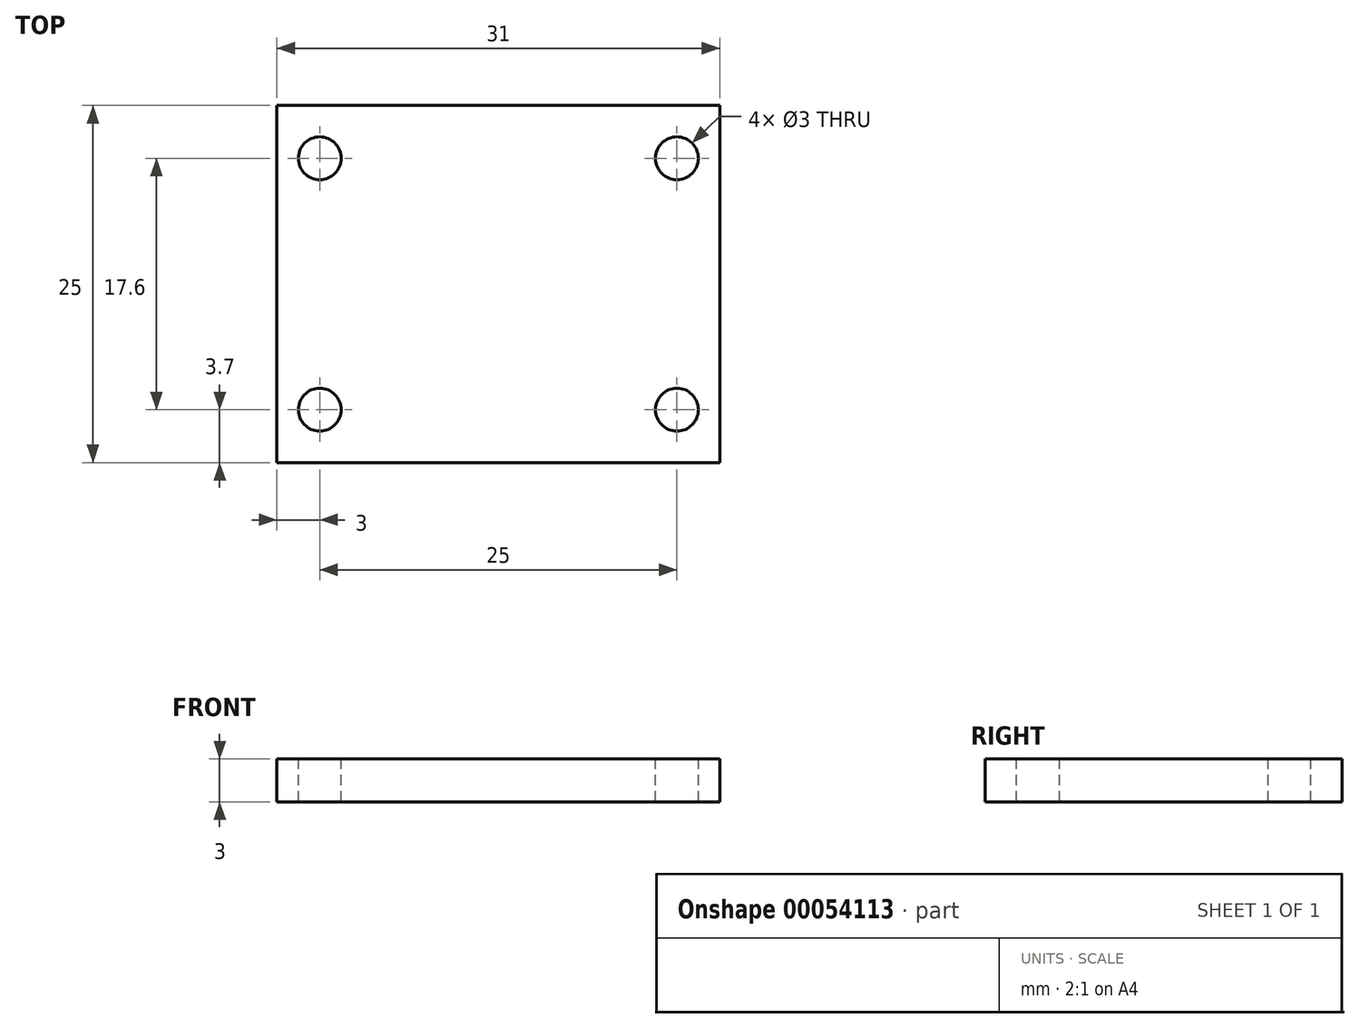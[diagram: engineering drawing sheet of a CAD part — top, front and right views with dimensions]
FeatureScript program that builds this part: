
annotation { "Feature Type Name" : "Feature", "Feature Type Description" : "" }
export const myFeature = defineFeature(function(context is Context, id is Id, definition is map)
    precondition{}
    {
        {
            var Q0;
            Q0=qCreatedBy(makeId("Top.planeOp"),FACE);
            var sketch = newSketch(context, id + "F0", { "sketchPlane" : qUnion([Q0])});
            skLineSegment(sketch, "E0.rect.bottom", {"start": v(15.5, 12.5) * mm, "end": v(-15.5, 12.5) * mm});
            skLineSegment(sketch, "E0.rect.top", {"start": v(15.5, -12.5) * mm, "end": v(-15.5, -12.5) * mm});
            skLineSegment(sketch, "E0.rect.left", {"start": v(15.5, 12.5) * mm, "end": v(15.5, -12.5) * mm});
            skLineSegment(sketch, "E0.rect.right", {"start": v(-15.5, 12.5) * mm, "end": v(-15.5, -12.5) * mm});
            skPoint(sketch, "E0.rect.middle", {"position": v(0, 0) * mm});
            skSolve(sketch);
        }
        {
            var Q0;
            Q0=makeQuery(id+"F0.imprint","IMPRINT",FACE,{"disambiguationData":[TD([[makeQuery(id+"F0.imprint","IMPRINT",EDGE,{"derivedFrom":sQuery(id+"F0.wireOp",EDGE,"E0.rect.bottom")}),1.0]])]});
            extrude(context, id + "F1", {"entities" : qUnion([Q0]), "depth" : 3 * mm});
        }
        {
            var Q0;
            Q0=makeQuery(id+"F1.opExtrude","CAP_FACE",FACE,{"disambiguationData":[OSD([sQuery(id+"F0.wireOp",EDGE,"E0.rect.bottom"),sQuery(id+"F0.wireOp",EDGE,"E0.rect.top"),sQuery(id+"F0.wireOp",EDGE,"E0.rect.left"),sQuery(id+"F0.wireOp",EDGE,"E0.rect.right")])],"isStart":false});
            var sketch = newSketch(context, id + "F2", { "sketchPlane" : qUnion([Q0])});
            skLineSegment(sketch, "E1", {"start": v(-15.5, 5.1) * mm, "end": v(15.5, 5.1) * mm, "construction": true});
            skLineSegment(sketch, "E2", {"start": v(15.5, -5.1) * mm, "end": v(-15.5, -5.1) * mm, "construction": true});
            skLineSegment(sketch, "E3", {"start": v(-15.5, 8.8) * mm, "end": v(15.5, 8.8) * mm, "construction": true});
            skLineSegment(sketch, "E4", {"start": v(15.5, -8.8) * mm, "end": v(-15.5, -8.8) * mm, "construction": true});
            skCircle(sketch, "E5", {"center": v(-12.5, 8.8) * mm, "radius": 1.5 * mm});
            skLineSegment(sketch, "E6", {"start": v(-15.5, 0) * mm, "end": v(15.5, 0) * mm, "construction": true});
            skCircle(sketch, "E7.MirrorC", {"center": v(-12.5, -8.8) * mm, "radius": 1.5 * mm});
            skLineSegment(sketch, "E8", {"start": v(0, 12.5) * mm, "end": v(0, -12.5) * mm, "construction": true});
            skCircle(sketch, "E9.MirrorC", {"center": v(12.5, 8.8) * mm, "radius": 1.5 * mm});
            skCircle(sketch, "E10.MirrorC", {"center": v(12.5, -8.8) * mm, "radius": 1.5 * mm});
            skSolve(sketch);
        }
        {
            var Q0;
            Q0 = qSketchRegion(id + "F2", true);
            extrude(context, id + "F3", {"entities" : qUnion([Q0]), "operationType" : NewBodyOperationType.REMOVE, "oppositeDirection" : true, "depth" : 25 * mm});
        }
    });
